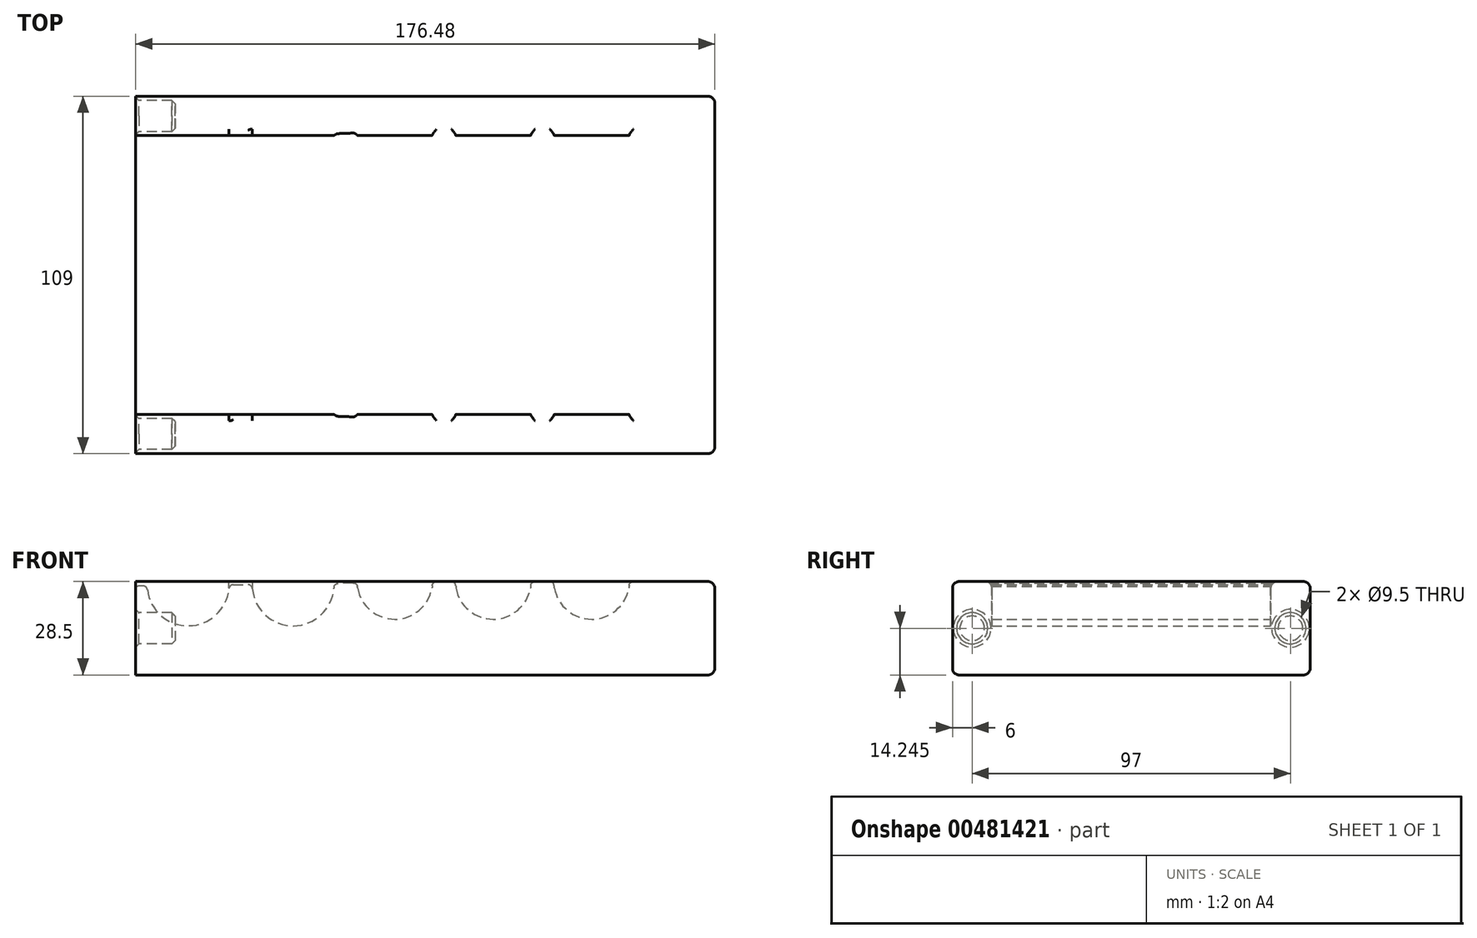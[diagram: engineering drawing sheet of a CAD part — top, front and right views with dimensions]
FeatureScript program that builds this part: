
annotation { "Feature Type Name" : "Feature", "Feature Type Description" : "" }
export const myFeature = defineFeature(function(context is Context, id is Id, definition is map)
    precondition{}
    {
        {
            var Q0;
            Q0=qCreatedBy(makeId("Front.planeOp"),FACE);
            var sketch = newSketch(context, id + "F0", { "sketchPlane" : qUnion([Q0])});
            skCircle(sketch, "E0", {"center": v(-244.97, -15.37) * mm, "radius": 17.5 * mm});
            skCircle(sketch, "E1", {"center": v(-203.98, -14.26) * mm, "radius": 16.5 * mm});
            skLineSegment(sketch, "E2.0", {"start": v(-288.47, 2.24) * mm, "end": v(100.45, 2.24) * mm});
            skCircle(sketch, "E3", {"center": v(-165, -13.26) * mm, "radius": 15.5 * mm});
            skCircle(sketch, "E4", {"center": v(-128, -12.26) * mm, "radius": 14.5 * mm});
            skCircle(sketch, "E5", {"center": v(-93.02, -11.26) * mm, "radius": 13.5 * mm});
            skCircle(sketch, "E6", {"center": v(-60.04, -10.26) * mm, "radius": 12.5 * mm});
            skCircle(sketch, "E7", {"center": v(-28.04, -10.26) * mm, "radius": 12.5 * mm});
            skCircle(sketch, "E8", {"center": v(2.95, -9.26) * mm, "radius": 11.5 * mm});
            skCircle(sketch, "E9", {"center": v(32.95, -9.26) * mm, "radius": 11.5 * mm});
            skCircle(sketch, "E10", {"center": v(62.95, -9.26) * mm, "radius": 11.5 * mm});
            skLineSegment(sketch, "E11", {"start": v(62.95, -9.26) * mm, "end": v(74.45, -9.26) * mm});
            skLineSegment(sketch, "E12", {"start": v(-244.97, -15.37) * mm, "end": v(-262.47, -15.37) * mm});
            skLineSegment(sketch, "E13", {"start": v(-244.97, -15.37) * mm, "end": v(-60.04, -10.26) * mm});
            skLineSegment(sketch, "E14", {"start": v(-60.04, -10.26) * mm, "end": v(-28.04, -10.26) * mm});
            skLineSegment(sketch, "E15", {"start": v(-28.04, -10.26) * mm, "end": v(2.95, -9.26) * mm});
            skLineSegment(sketch, "E16", {"start": v(2.95, -9.26) * mm, "end": v(62.95, -9.26) * mm});
            skLineSegment(sketch, "E17", {"start": v(-288.47, 2.24) * mm, "end": v(-288.47, -37.76) * mm});
            skLineSegment(sketch, "E18", {"start": v(-288.47, -37.76) * mm, "end": v(100.45, -37.76) * mm});
            skLineSegment(sketch, "E19", {"start": v(100.45, -37.76) * mm, "end": v(100.45, 2.24) * mm});
            skLineSegment(sketch, "E20", {"start": v(-262.47, -15.37) * mm, "end": v(-262.47, 2.24) * mm});
            skLineSegment(sketch, "E21", {"start": v(74.45, -9.26) * mm, "end": v(74.45, 2.24) * mm});
            skSolve(sketch);
        }
        {
            var Q0;
            {var subQ17=sQuery(id+"F0.wireOp",EDGE,"E17");Q0=makeQuery(id+"F0.imprint","IMPRINT",FACE,{"disambiguationData":[TD([[makeQuery(id+"F0.imprint","IMPRINT",EDGE,{"derivedFrom":subQ17}),1.0]])]});}
            extrude(context, id + "F1", {"entities" : qUnion([Q0]), "depth" : 85 * mm});
        }
        {
            var Q0;
            Q0=makeQuery(id+"F1.opExtrude","CAP_FACE",FACE,{"disambiguationData":[OSD([sQuery(id+"F0.wireOp",EDGE,"E0"),sQuery(id+"F0.wireOp",EDGE,"E1"),sQuery(id+"F0.wireOp",EDGE,"E2.0"),sQuery(id+"F0.wireOp",EDGE,"E3"),sQuery(id+"F0.wireOp",EDGE,"E4"),sQuery(id+"F0.wireOp",EDGE,"E5"),sQuery(id+"F0.wireOp",EDGE,"E6"),sQuery(id+"F0.wireOp",EDGE,"E7"),sQuery(id+"F0.wireOp",EDGE,"E8"),sQuery(id+"F0.wireOp",EDGE,"E9"),sQuery(id+"F0.wireOp",EDGE,"E10"),sQuery(id+"F0.wireOp",EDGE,"E13"),sQuery(id+"F0.wireOp",EDGE,"E14"),sQuery(id+"F0.wireOp",EDGE,"E15"),sQuery(id+"F0.wireOp",EDGE,"E16"),sQuery(id+"F0.wireOp",EDGE,"E17"),sQuery(id+"F0.wireOp",EDGE,"E18"),sQuery(id+"F0.wireOp",EDGE,"E19"),sQuery(id+"F0.wireOp",EDGE,"E20"),sQuery(id+"F0.wireOp",EDGE,"E21")])],"isStart":false});
            var sketch = newSketch(context, id + "F2", { "sketchPlane" : qUnion([Q0])});
            skLineSegment(sketch, "E22.0", {"start": v(-288.47, -37.76) * mm, "end": v(100.45, -37.76) * mm});
            skLineSegment(sketch, "E23.0", {"start": v(-288.47, 2.24) * mm, "end": v(-288.47, -37.76) * mm});
            skLineSegment(sketch, "E24.0", {"start": v(100.45, -37.76) * mm, "end": v(100.45, 2.24) * mm});
            skLineSegment(sketch, "E25", {"start": v(100.45, 2.24) * mm, "end": v(-288.47, 2.24) * mm});
            skSolve(sketch);
        }
        {
            var Q0;
            Q0 = qSketchRegion(id + "F2", true);
            extrude(context, id + "F3", {"entities" : qUnion([Q0]), "operationType" : NewBodyOperationType.ADD, "depth" : 12 * mm});
        }
        {
            var Q0;
            Q0=makeQuery(id+"F1.opExtrude","CAP_FACE",FACE,{"disambiguationData":[OSD([sQuery(id+"F0.wireOp",EDGE,"E0"),sQuery(id+"F0.wireOp",EDGE,"E1"),sQuery(id+"F0.wireOp",EDGE,"E2.0"),sQuery(id+"F0.wireOp",EDGE,"E3"),sQuery(id+"F0.wireOp",EDGE,"E4"),sQuery(id+"F0.wireOp",EDGE,"E5"),sQuery(id+"F0.wireOp",EDGE,"E6"),sQuery(id+"F0.wireOp",EDGE,"E7"),sQuery(id+"F0.wireOp",EDGE,"E8"),sQuery(id+"F0.wireOp",EDGE,"E9"),sQuery(id+"F0.wireOp",EDGE,"E10"),sQuery(id+"F0.wireOp",EDGE,"E13"),sQuery(id+"F0.wireOp",EDGE,"E14"),sQuery(id+"F0.wireOp",EDGE,"E15"),sQuery(id+"F0.wireOp",EDGE,"E16"),sQuery(id+"F0.wireOp",EDGE,"E17"),sQuery(id+"F0.wireOp",EDGE,"E18"),sQuery(id+"F0.wireOp",EDGE,"E19"),sQuery(id+"F0.wireOp",EDGE,"E20"),sQuery(id+"F0.wireOp",EDGE,"E21")])],"isStart":true});
            var sketch = newSketch(context, id + "F4", { "sketchPlane" : qUnion([Q0])});
            skLineSegment(sketch, "E26.0", {"start": v(-100.45, -37.76) * mm, "end": v(-100.45, 2.24) * mm});
            skLineSegment(sketch, "E27.0", {"start": v(288.47, -37.76) * mm, "end": v(-100.45, -37.76) * mm});
            skLineSegment(sketch, "E28.0", {"start": v(288.47, 2.24) * mm, "end": v(288.47, -37.76) * mm});
            skLineSegment(sketch, "E29", {"start": v(288.47, 2.24) * mm, "end": v(-100.45, 2.24) * mm});
            skSolve(sketch);
        }
        {
            var Q0;
            Q0 = qSketchRegion(id + "F4", true);
            extrude(context, id + "F5", {"entities" : qUnion([Q0]), "operationType" : NewBodyOperationType.ADD, "depth" : 12 * mm});
        }
        {
            var Q0;
            {var subQ0=sQuery(id+"F0.wireOp",EDGE,"E2.0");Q0=makeQuery(id+"F5.boolean.opBoolean","MERGE",FACE,{"derivedFrom":[makeQuery(id+"F3.boolean.opBoolean","MERGE",FACE,{"derivedFrom":[makeQuery(id+"F1.opExtrude","SWEPT_FACE",FACE,{"disambiguationData":[OSD([subQ0]),TDD([makeQuery(id+"F0.imprint","IMPRINT",EDGE,{"disambiguationData":[TD([[makeQuery(id+"F0.imprint","INTERSECT",VERTEX,{"derivedFrom":[subQ0,sQuery(id+"F0.wireOp",EDGE,"E17")]}),-1.0]])],"derivedFrom":subQ0})])]}),makeQuery(id+"F1.opExtrude","SWEPT_FACE",FACE,{"disambiguationData":[OSD([subQ0]),TDD([makeQuery(id+"F0.imprint","IMPRINT",EDGE,{"disambiguationData":[TD([[makeQuery(id+"F0.imprint","INTERSECT",VERTEX,{"derivedFrom":[subQ0,sQuery(id+"F0.wireOp",EDGE,"E19")]}),1.0]])],"derivedFrom":subQ0})])]}),makeQuery(id+"F3.opExtrude","SWEPT_FACE",FACE,{"disambiguationData":[OSD([sQuery(id+"F2.wireOp",EDGE,"E25")])]})]}),makeQuery(id+"F5.opExtrude","SWEPT_FACE",FACE,{"disambiguationData":[OSD([sQuery(id+"F4.wireOp",EDGE,"E29")])]})]});}
            var sketch = newSketch(context, id + "F6", { "sketchPlane" : qUnion([Q0])});
            skLineSegment(sketch, "E30.0", {"start": v(-72.53, -85) * mm, "end": v(-72.53, 0) * mm});
            skLineSegment(sketch, "E31.0", {"start": v(-79.53, -85) * mm, "end": v(-79.53, 0) * mm});
            skLineSegment(sketch, "E32", {"start": v(-76.03, 0) * mm, "end": v(-72.53, 0) * mm});
            skLineSegment(sketch, "E33", {"start": v(-76.03, 0) * mm, "end": v(-76.03, 21.68) * mm});
            skLineSegment(sketch, "E34", {"start": v(-76.03, 0) * mm, "end": v(-76.03, -105.38) * mm});
            skLineSegment(sketch, "E35", {"start": v(-76.03, -105.38) * mm, "end": v(-288.47, -105.38) * mm});
            skLineSegment(sketch, "E36", {"start": v(-76.03, 21.68) * mm, "end": v(-288.47, 21.68) * mm});
            skLineSegment(sketch, "E37", {"start": v(-288.47, -105.38) * mm, "end": v(-288.47, 21.68) * mm});
            skSolve(sketch);
        }
        {
            var Q0;
            Q0 = qSketchRegion(id + "F6", true);
            extrude(context, id + "F7", {"entities" : qUnion([Q0]), "operationType" : NewBodyOperationType.REMOVE, "endBound" : BoundingType.THROUGH_ALL, "oppositeDirection" : true, "depth" : 25 * mm, "offsetDistance" : 25 * mm});
        }
        {
            var Q0;
            Q0=makeQuery(id+"F7.boolean.opBoolean","COPY",FACE,{"derivedFrom":makeQuery(id+"F7.opExtrude","SWEPT_FACE",FACE,{"disambiguationData":[OSD([sQuery(id+"F6.wireOp",EDGE,"E33"),sQuery(id+"F6.wireOp",EDGE,"E34")])]})});
            var sketch = newSketch(context, id + "F8", { "sketchPlane" : qUnion([Q0])});
            skLineSegment(sketch, "E38", {"start": v(-6, -23.51) * mm, "end": v(-6, -37.76) * mm});
            skLineSegment(sketch, "E39", {"start": v(91, -23.51) * mm, "end": v(91, -37.76) * mm});
            skCircle(sketch, "E40", {"center": v(-6, -23.51) * mm, "radius": 4.75 * mm});
            skCircle(sketch, "E41", {"center": v(91, -23.51) * mm, "radius": 4.75 * mm});
            skSolve(sketch);
        }
        {
            var Q0;
            Q0 = qSketchRegion(id + "F8", true);
            extrude(context, id + "F9", {"entities" : qUnion([Q0]), "operationType" : NewBodyOperationType.REMOVE, "oppositeDirection" : true, "depth" : 12 * mm, "offsetDistance" : 25 * mm});
        }
        {
            var Q0;
            Q0=makeQuery(id+"F9.boolean.opBoolean","COPY",FACE,{"derivedFrom":makeQuery(id+"F9.opExtrude","SWEPT_FACE",FACE,{"disambiguationData":[OSD([sQuery(id+"F8.wireOp",EDGE,"E40")])]})});
            var Q1;
            Q1=makeQuery(id+"F9.boolean.opBoolean","COPY",FACE,{"derivedFrom":makeQuery(id+"F9.opExtrude","SWEPT_FACE",FACE,{"disambiguationData":[OSD([sQuery(id+"F8.wireOp",EDGE,"E41")])]})});
            chamfer(context, id + "F10", {"entities" : qUnion([Q0, Q1]), "width" : 1 * mm, "tangentPropagation" : true});
        }
        {
            var Q0;
            Q0=makeQuery(id+"F7.boolean.opBoolean","COPY",FACE,{"derivedFrom":makeQuery(id+"F7.opExtrude","SWEPT_FACE",FACE,{"disambiguationData":[OSD([sQuery(id+"F6.wireOp",EDGE,"E33"),sQuery(id+"F6.wireOp",EDGE,"E34")])]})});
            var sketch = newSketch(context, id + "F11", { "sketchPlane" : qUnion([Q0])});
            skLineSegment(sketch, "E42.0", {"start": v(97, -37.76) * mm, "end": v(-12, -37.76) * mm});
            skLineSegment(sketch, "E43", {"start": v(-21.08, -37.76) * mm, "end": v(-21.08, -9.26) * mm});
            skLineSegment(sketch, "E44", {"start": v(-21.08, -9.26) * mm, "end": v(105.21, -9.26) * mm});
            skLineSegment(sketch, "E45", {"start": v(105.21, -9.26) * mm, "end": v(105.21, 2.24) * mm});
            skLineSegment(sketch, "E46", {"start": v(105.21, 2.24) * mm, "end": v(-21.08, 2.24) * mm});
            skLineSegment(sketch, "E47", {"start": v(-21.08, 2.24) * mm, "end": v(-21.08, -9.26) * mm});
            skSolve(sketch);
        }
        {
            var Q0;
            Q0 = qSketchRegion(id + "F11", true);
            extrude(context, id + "F12", {"entities" : qUnion([Q0]), "operationType" : NewBodyOperationType.REMOVE, "endBound" : BoundingType.THROUGH_ALL, "oppositeDirection" : true, "depth" : 25 * mm, "offsetDistance" : 25 * mm});
        }
        {
            var Q0;
            Q0=makeQuery(id+"F1.opExtrude","SWEPT_EDGE",EDGE,{"disambiguationData":[OSD([sQuery(id+"F0.wireOp",EDGE,"E6"),sQuery(id+"F0.wireOp",EDGE,"E13")])]});
            var Q1;
            Q1=makeQuery(id+"F1.opExtrude","SWEPT_EDGE",EDGE,{"disambiguationData":[OSD([sQuery(id+"F0.wireOp",EDGE,"E6"),sQuery(id+"F0.wireOp",EDGE,"E14")])]});
            var Q2;
            Q2=makeQuery(id+"F1.opExtrude","SWEPT_EDGE",EDGE,{"disambiguationData":[OSD([sQuery(id+"F0.wireOp",EDGE,"E7"),sQuery(id+"F0.wireOp",EDGE,"E14")])]});
            var Q3;
            Q3=makeQuery(id+"F1.opExtrude","SWEPT_EDGE",EDGE,{"disambiguationData":[OSD([sQuery(id+"F0.wireOp",EDGE,"E7"),sQuery(id+"F0.wireOp",EDGE,"E15")])]});
            var Q4;
            Q4=makeQuery(id+"F1.opExtrude","SWEPT_EDGE",EDGE,{"disambiguationData":[OSD([sQuery(id+"F0.wireOp",EDGE,"E8"),sQuery(id+"F0.wireOp",EDGE,"E15")])]});
            var Q5;
            Q5=makeQuery(id+"F1.opExtrude","SWEPT_EDGE",EDGE,{"disambiguationData":[OSD([sQuery(id+"F0.wireOp",EDGE,"E8"),sQuery(id+"F0.wireOp",EDGE,"E16")])]});
            var Q6;
            {var subQ0=sQuery(id+"F0.wireOp",EDGE,"E16");var subQ1=sQuery(id+"F0.wireOp",EDGE,"E9");Q6=makeQuery(id+"F1.opExtrude","SWEPT_EDGE",EDGE,{"disambiguationData":[OSD([subQ1,subQ0]),TDD([makeQuery(id+"F0.imprint","INTERSECT",VERTEX,{"disambiguationData":[OD(1.0)],"derivedFrom":[subQ1,subQ0]})])]});}
            var Q7;
            {var subQ0=sQuery(id+"F0.wireOp",EDGE,"E16");var subQ1=sQuery(id+"F0.wireOp",EDGE,"E9");Q7=makeQuery(id+"F1.opExtrude","SWEPT_EDGE",EDGE,{"disambiguationData":[OSD([subQ1,subQ0]),TDD([makeQuery(id+"F0.imprint","INTERSECT",VERTEX,{"disambiguationData":[OD(0.0)],"derivedFrom":[subQ1,subQ0]})])]});}
            var Q8;
            Q8=makeQuery(id+"F1.opExtrude","SWEPT_EDGE",EDGE,{"disambiguationData":[OSD([sQuery(id+"F0.wireOp",EDGE,"E10"),sQuery(id+"F0.wireOp",EDGE,"E16")])]});
            var Q9;
            Q9=makeQuery(id+"F1.opExtrude","SWEPT_EDGE",EDGE,{"disambiguationData":[OSD([sQuery(id+"F0.wireOp",EDGE,"E10"),sQuery(id+"F0.wireOp",EDGE,"E11"),sQuery(id+"F0.wireOp",EDGE,"E21")])]});
            fillet(context, id + "F13", {"entities" : qUnion([Q0, Q1, Q2, Q3, Q4, Q5, Q6, Q7, Q8, Q9]), "radius" : 1.3 * mm, "tangentPropagation" : true, "allowEdgeOverflow" : false});
        }
        {
            var Q0;
            Q0=makeQuery(id+"F5.boolean.opBoolean","MERGE",FACE,{"derivedFrom":[makeQuery(id+"F3.boolean.opBoolean","MERGE",FACE,{"derivedFrom":[makeQuery(id+"F1.opExtrude","SWEPT_FACE",FACE,{"disambiguationData":[OSD([sQuery(id+"F0.wireOp",EDGE,"E19")])]}),makeQuery(id+"F3.opExtrude","SWEPT_FACE",FACE,{"disambiguationData":[OSD([sQuery(id+"F2.wireOp",EDGE,"E24.0")])]})]}),makeQuery(id+"F5.opExtrude","SWEPT_FACE",FACE,{"disambiguationData":[OSD([sQuery(id+"F4.wireOp",EDGE,"E26.0")])]})]});
            var Q1;
            Q1=makeQuery(id+"F12.boolean.opBoolean","INTERSECT",EDGE,{"disambiguationData":[OD(2.0)],"derivedFrom":[makeQuery(id+"F5.opExtrude","CAP_FACE",FACE,{"disambiguationData":[OSD([sQuery(id+"F4.wireOp",EDGE,"E26.0"),sQuery(id+"F4.wireOp",EDGE,"E27.0"),sQuery(id+"F4.wireOp",EDGE,"E28.0"),sQuery(id+"F4.wireOp",EDGE,"E29")])],"isStart":true}),makeQuery(id+"F12.opExtrude","SWEPT_FACE",FACE,{"disambiguationData":[OSD([sQuery(id+"F11.wireOp",EDGE,"E44")])]})]});
            var Q2;
            Q2=makeQuery(id+"F12.boolean.opBoolean","INTERSECT",EDGE,{"disambiguationData":[OD(2.0)],"derivedFrom":[makeQuery(id+"F3.opExtrude","CAP_FACE",FACE,{"disambiguationData":[OSD([sQuery(id+"F2.wireOp",EDGE,"E22.0"),sQuery(id+"F2.wireOp",EDGE,"E23.0"),sQuery(id+"F2.wireOp",EDGE,"E24.0"),sQuery(id+"F2.wireOp",EDGE,"E25")])],"isStart":true}),makeQuery(id+"F12.opExtrude","SWEPT_FACE",FACE,{"disambiguationData":[OSD([sQuery(id+"F11.wireOp",EDGE,"E44")])]})]});
            var Q3;
            Q3=makeQuery(id+"F12.boolean.opBoolean","INTERSECT",EDGE,{"disambiguationData":[OD(1.0)],"derivedFrom":[makeQuery(id+"F3.opExtrude","CAP_FACE",FACE,{"disambiguationData":[OSD([sQuery(id+"F2.wireOp",EDGE,"E22.0"),sQuery(id+"F2.wireOp",EDGE,"E23.0"),sQuery(id+"F2.wireOp",EDGE,"E24.0"),sQuery(id+"F2.wireOp",EDGE,"E25")])],"isStart":true}),makeQuery(id+"F12.opExtrude","SWEPT_FACE",FACE,{"disambiguationData":[OSD([sQuery(id+"F11.wireOp",EDGE,"E44")])]})]});
            var Q4;
            Q4=makeQuery(id+"F12.boolean.opBoolean","INTERSECT",EDGE,{"disambiguationData":[OD(0.0)],"derivedFrom":[makeQuery(id+"F3.opExtrude","CAP_FACE",FACE,{"disambiguationData":[OSD([sQuery(id+"F2.wireOp",EDGE,"E22.0"),sQuery(id+"F2.wireOp",EDGE,"E23.0"),sQuery(id+"F2.wireOp",EDGE,"E24.0"),sQuery(id+"F2.wireOp",EDGE,"E25")])],"isStart":true}),makeQuery(id+"F12.opExtrude","SWEPT_FACE",FACE,{"disambiguationData":[OSD([sQuery(id+"F11.wireOp",EDGE,"E44")])]})]});
            var Q5;
            Q5=makeQuery(id+"F12.boolean.opBoolean","INTERSECT",EDGE,{"disambiguationData":[OD(0.0)],"derivedFrom":[makeQuery(id+"F5.opExtrude","CAP_FACE",FACE,{"disambiguationData":[OSD([sQuery(id+"F4.wireOp",EDGE,"E26.0"),sQuery(id+"F4.wireOp",EDGE,"E27.0"),sQuery(id+"F4.wireOp",EDGE,"E28.0"),sQuery(id+"F4.wireOp",EDGE,"E29")])],"isStart":true}),makeQuery(id+"F12.opExtrude","SWEPT_FACE",FACE,{"disambiguationData":[OSD([sQuery(id+"F11.wireOp",EDGE,"E44")])]})]});
            var Q6;
            Q6=makeQuery(id+"F12.boolean.opBoolean","INTERSECT",EDGE,{"disambiguationData":[OD(1.0)],"derivedFrom":[makeQuery(id+"F5.opExtrude","CAP_FACE",FACE,{"disambiguationData":[OSD([sQuery(id+"F4.wireOp",EDGE,"E26.0"),sQuery(id+"F4.wireOp",EDGE,"E27.0"),sQuery(id+"F4.wireOp",EDGE,"E28.0"),sQuery(id+"F4.wireOp",EDGE,"E29")])],"isStart":true}),makeQuery(id+"F12.opExtrude","SWEPT_FACE",FACE,{"disambiguationData":[OSD([sQuery(id+"F11.wireOp",EDGE,"E44")])]})]});
            var Q7;
            Q7=makeQuery(id+"F12.boolean.opBoolean","INTERSECT",EDGE,{"derivedFrom":[makeQuery(id+"F3.opExtrude","CAP_FACE",FACE,{"disambiguationData":[OSD([sQuery(id+"F2.wireOp",EDGE,"E22.0"),sQuery(id+"F2.wireOp",EDGE,"E23.0"),sQuery(id+"F2.wireOp",EDGE,"E24.0"),sQuery(id+"F2.wireOp",EDGE,"E25")])],"isStart":false}),makeQuery(id+"F12.opExtrude","SWEPT_FACE",FACE,{"disambiguationData":[OSD([sQuery(id+"F11.wireOp",EDGE,"E44")])]})]});
            var Q8;
            Q8=makeQuery(id+"F3.opExtrude","CAP_EDGE",EDGE,{"disambiguationData":[OSD([sQuery(id+"F2.wireOp",EDGE,"E22.0")])],"isStart":false});
            var Q9;
            Q9=makeQuery(id+"F12.boolean.opBoolean","INTERSECT",EDGE,{"derivedFrom":[makeQuery(id+"F5.opExtrude","CAP_FACE",FACE,{"disambiguationData":[OSD([sQuery(id+"F4.wireOp",EDGE,"E26.0"),sQuery(id+"F4.wireOp",EDGE,"E27.0"),sQuery(id+"F4.wireOp",EDGE,"E28.0"),sQuery(id+"F4.wireOp",EDGE,"E29")])],"isStart":false}),makeQuery(id+"F12.opExtrude","SWEPT_FACE",FACE,{"disambiguationData":[OSD([sQuery(id+"F11.wireOp",EDGE,"E44")])]})]});
            var Q10;
            Q10=makeQuery(id+"F5.opExtrude","CAP_EDGE",EDGE,{"disambiguationData":[OSD([sQuery(id+"F4.wireOp",EDGE,"E27.0")])],"isStart":false});
            fillet(context, id + "F14", {"entities" : qUnion([Q0, Q1, Q2, Q3, Q4, Q5, Q6, Q7, Q8, Q9, Q10]), "radius" : 2 * mm, "tangentPropagation" : true, "allowEdgeOverflow" : false});
        }
    });
